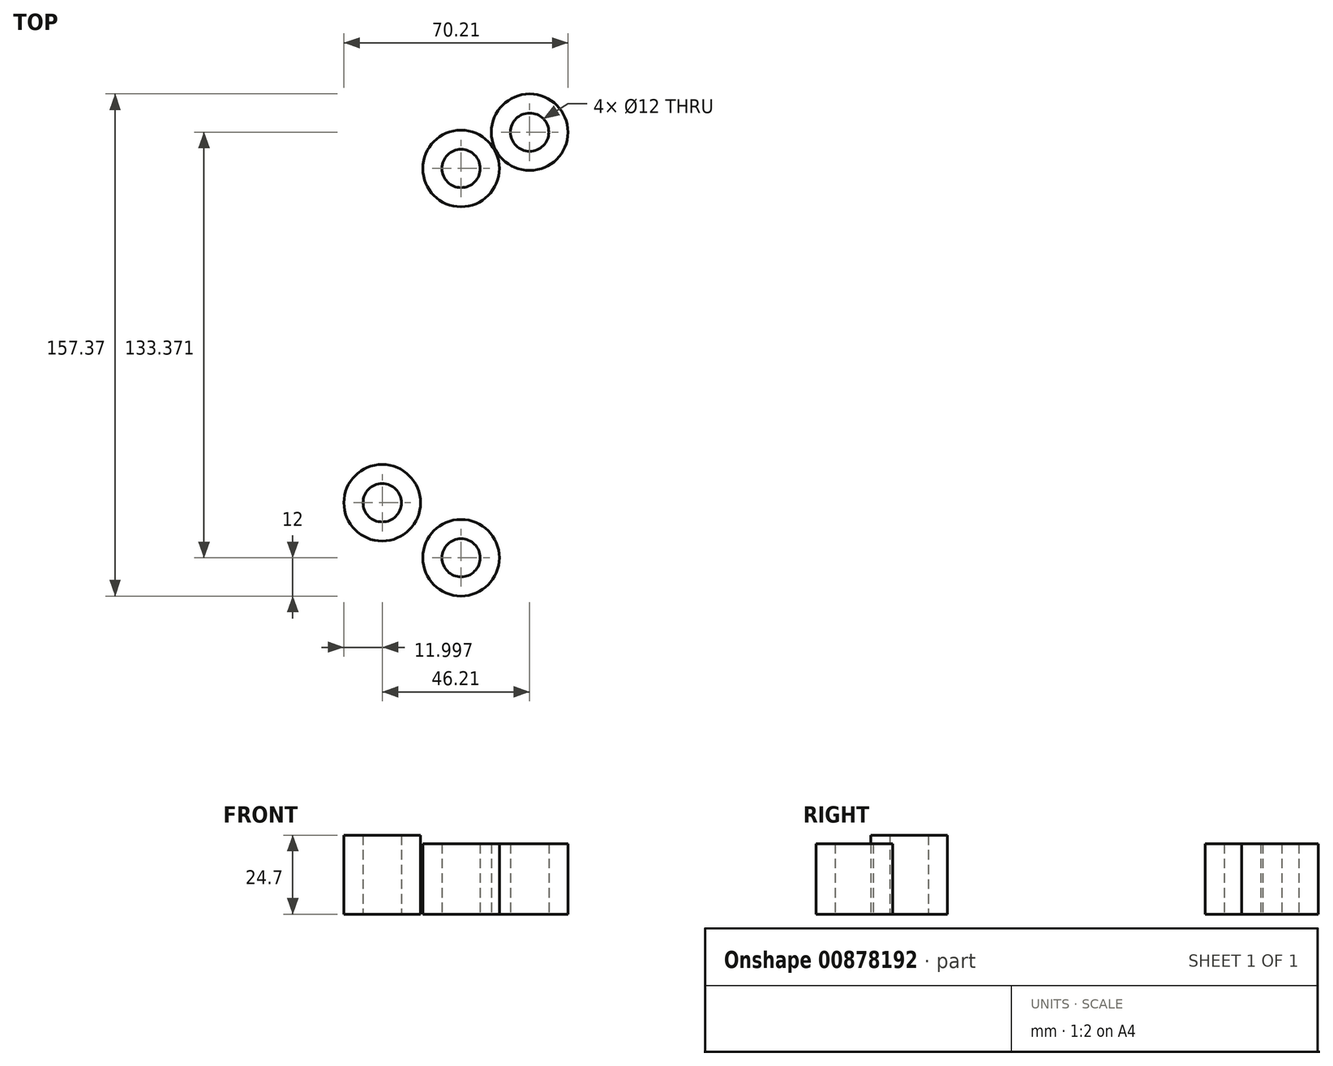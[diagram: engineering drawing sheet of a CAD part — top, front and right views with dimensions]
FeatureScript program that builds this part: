
annotation { "Feature Type Name" : "Feature", "Feature Type Description" : "" }
export const myFeature = defineFeature(function(context is Context, id is Id, definition is map)
    precondition{}
    {
        {
            var Q0;
            Q0=qCreatedBy(makeId("Top.planeOp"),FACE);
            var sketch = newSketch(context, id + "F0", { "sketchPlane" : qUnion([Q0])});
            skCircle(sketch, "E0", {"center": v(0, 0) * mm, "radius": 73.5 * mm, "construction": true});
            skCircle(sketch, "E1", {"center": v(0, 0) * mm, "radius": 70 * mm, "construction": true});
            skCircle(sketch, "E2", {"center": v(-34.34, 61) * mm, "radius": 6 * mm});
            skCircle(sketch, "E3", {"center": v(-34.34, -61) * mm, "radius": 6 * mm});
            skCircle(sketch, "E4", {"center": v(-59.04, -43.77) * mm, "radius": 6 * mm});
            skCircle(sketch, "E5", {"center": v(-12.83, 72.37) * mm, "radius": 6 * mm});
            skLineSegment(sketch, "E6", {"start": v(-12.83, 72.37) * mm, "end": v(-59.04, -43.77) * mm, "construction": true});
            skLineSegment(sketch, "E7", {"start": v(-34.34, 61) * mm, "end": v(-34.34, -61) * mm, "construction": true});
            skCircle(sketch, "E8", {"center": v(-59.04, -43.77) * mm, "radius": 12 * mm});
            skCircle(sketch, "E9", {"center": v(-34.34, -61) * mm, "radius": 12 * mm});
            skCircle(sketch, "E10", {"center": v(-12.83, 72.37) * mm, "radius": 12 * mm});
            skCircle(sketch, "E11", {"center": v(-34.34, 61) * mm, "radius": 12 * mm});
            skLineSegment(sketch, "E12", {"start": v(-34.34, -61) * mm, "end": v(-22.34, -61) * mm});
            skLineSegment(sketch, "E13", {"start": v(-22.34, -61) * mm, "end": v(-22.34, 51.12) * mm});
            skPoint(sketch, "E14.start.orphan", {"position": v(-22.34, 61) * mm});
            skCircle(sketch, "E15", {"center": v(-77.12, -16.16) * mm, "radius": 2.5 * mm});
            skCircle(sketch, "E16", {"center": v(-47.8, 73.73) * mm, "radius": 2.5 * mm});
            skLineSegment(sketch, "E17", {"start": v(-77.12, -16.16) * mm, "end": v(-47.8, 73.73) * mm, "construction": true});
            skLineSegment(sketch, "E18", {"start": v(-59.04, -43.77) * mm, "end": v(-84.13, -33.8) * mm, "construction": true});
            skLineSegment(sketch, "E19", {"start": v(-84.13, -33.8) * mm, "end": v(-77.12, -16.16) * mm, "construction": true});
            skLineSegment(sketch, "E20", {"start": v(-59.04, -43.77) * mm, "end": v(-77.12, -16.16) * mm, "construction": true});
            skLineSegment(sketch, "E21", {"start": v(-12.83, 72.37) * mm, "end": v(-43.5, 84.57) * mm, "construction": true});
            skLineSegment(sketch, "E22", {"start": v(-43.5, 84.57) * mm, "end": v(-47.8, 73.73) * mm, "construction": true});
            skLineSegment(sketch, "E23", {"start": v(-12.83, 72.37) * mm, "end": v(-47.8, 73.73) * mm, "construction": true});
            skCircle(sketch, "E24", {"center": v(-62.46, 28.79) * mm, "radius": 40 * mm});
            skSolve(sketch);
        }
        {
            var Q0;
            Q0=makeQuery(id+"F0.imprint","IMPRINT",FACE,{"disambiguationData":[TD([[makeQuery(id+"F0.imprint","IMPRINT",EDGE,{"derivedFrom":sQuery(id+"F0.wireOp",EDGE,"E2")}),-1.0]])]});
            var Q1;
            Q1=makeQuery(id+"F0.imprint","IMPRINT",FACE,{"disambiguationData":[TD([[makeQuery(id+"F0.imprint","IMPRINT",EDGE,{"derivedFrom":sQuery(id+"F0.wireOp",EDGE,"E3")}),-1.0]])]});
            var Q2;
            {var subQ0=sQuery(id+"F0.wireOp",EDGE,"uvAYMqGV-DIzJ-fmoX-Jquh-CrT9dVzAXWpi");Q2=makeQuery(id+"F0.imprint","IMPRINT",FACE,{"disambiguationData":[TD([[makeQuery(id+"F0.imprint","IMPRINT",EDGE,{"derivedFrom":subQ0}),1.0]])]});}
            var Q3;
            Q3=makeQuery(id+"F0.imprint","IMPRINT",FACE,{"disambiguationData":[TD([[makeQuery(id+"F0.imprint","IMPRINT",EDGE,{"derivedFrom":sQuery(id+"F0.wireOp",EDGE,"E5")}),-1.0]])]});
            var Q4;
            {var subQ0=sQuery(id+"F0.wireOp",EDGE,"5625360e-2d45-4daa-a3da-605d3618f61e.trimOffspring");Q4=makeQuery(id+"F0.imprint","IMPRINT",FACE,{"disambiguationData":[TD([[makeQuery(id+"F0.imprint","IMPRINT",EDGE,{"derivedFrom":subQ0}),1.0]])]});}
            var Q5;
            {var subQ8=sQuery(id+"F0.wireOp",EDGE,"UsUqNIiJ-VfbJ-wgNQ-Aa4I-qdWGud0cX9Ic");Q5=makeQuery(id+"F0.imprint","IMPRINT",FACE,{"disambiguationData":[TD([[makeQuery(id+"F0.imprint","IMPRINT",EDGE,{"derivedFrom":subQ8}),1.0]])]});}
            var Q6;
            {var subQ5=sQuery(id+"F0.wireOp",EDGE,"7202584b-8c20-40f0-bc9d-29dd12e960fb.trimOffspring");Q6=makeQuery(id+"F0.imprint","IMPRINT",FACE,{"disambiguationData":[TD([[makeQuery(id+"F0.imprint","IMPRINT",EDGE,{"derivedFrom":subQ5}),-1.0]])]});}
            extrude(context, id + "F1", {"entities" : qUnion([Q0, Q1, Q2, Q3, Q4, Q5, Q6]), "depth" : 22 * mm, "offsetDistance" : 25 * mm});
        }
        {
            var Q0;
            Q0=makeQuery(id+"F0.imprint","IMPRINT",FACE,{"disambiguationData":[TD([[makeQuery(id+"F0.imprint","IMPRINT",EDGE,{"derivedFrom":sQuery(id+"F0.wireOp",EDGE,"E4")}),-1.0]])]});
            extrude(context, id + "F2", {"entities" : qUnion([Q0]), "operationType" : NewBodyOperationType.ADD, "depth" : 24.7 * mm, "offsetDistance" : 25 * mm});
        }
    });
